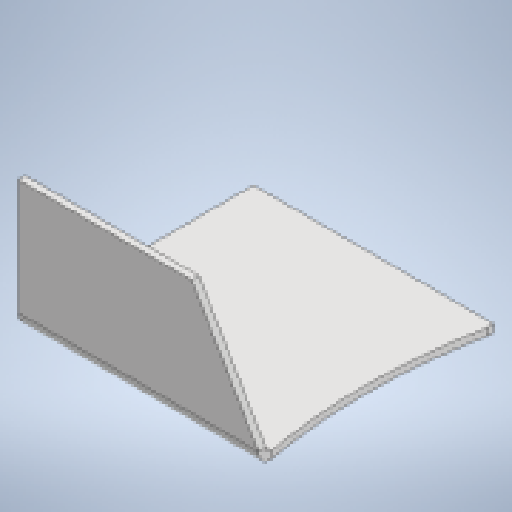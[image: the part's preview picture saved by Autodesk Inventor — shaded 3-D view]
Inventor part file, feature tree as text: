
AUTODESK INVENTOR PART (.ipt)
format: ipt  version: 2025.4 (Build 294407000, 407)  size: 206,336 bytes
history: native  units: mm
features: sheet_metal_op x4, other x4, sketch x3, projected_geometry x1
ambient origin geometry x8: Origin, YZ Plane, XZ Plane, XY Plane, X Axis, Y Axis, Z Axis, Center Point
bodies: Body1 (feature_tree)
feature tree (12):
  sheet_metal_op  "Face2"
  sheet_metal_op  "Flange1"
  sketch  "Sketch2"  dims[d14=6.0mm]
  other  "Plate2"
  sketch  "Sketch5"  dims[d29=200.0mm]
  other  "Plate3"
  sheet_metal_op  "Bend1"
  sheet_metal_op  "Corner1"
  sketch  "Sketch6"  dims[d30=200.0mm d31=5.0mm d32=5.0mm d33=480.0mm d34=6.0mm d35=3.0mm d36=12.0mm d37=6.0mm d38=110.0mm d39=90.0deg d40=6.0mm d41=24.0mm d42=6.0mm d43=6.0mm d44=30.0deg d45=6.0mm d46=0.0mm]
  projected_geometry  "Projected Loop1"
  other  "Cut3"
  other  "Definition1"
